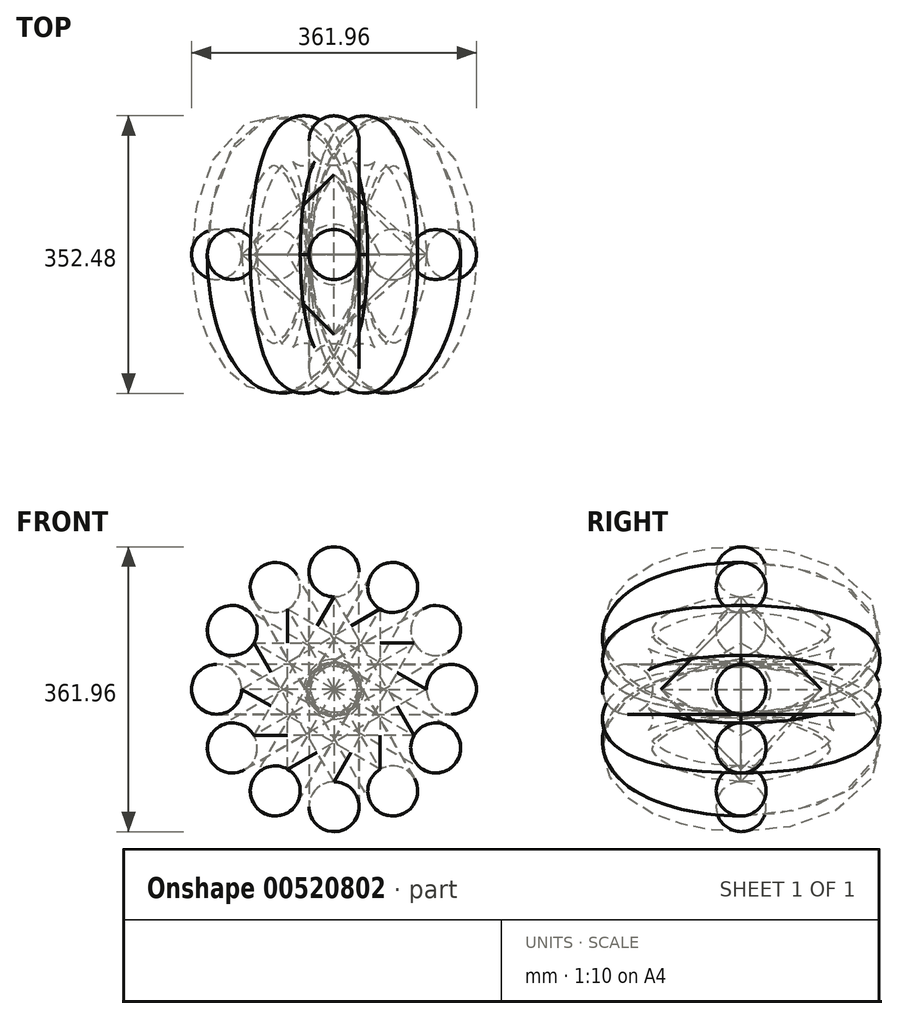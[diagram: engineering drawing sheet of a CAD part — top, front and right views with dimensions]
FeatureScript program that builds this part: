
annotation { "Feature Type Name" : "Feature", "Feature Type Description" : "" }
export const myFeature = defineFeature(function(context is Context, id is Id, definition is map)
    precondition{}
    {
        {
            var Q0;
            Q0=qCreatedBy(makeId("Front.planeOp"),FACE);
            var sketch = newSketch(context, id + "F0", { "sketchPlane" : qUnion([Q0])});
            skCircle(sketch, "E0.cCircle", {"center": v(0, 0) * mm, "radius": 180.98 * mm});
            skLineSegment(sketch, "E0.0", {"start": v(48.5, -180.98) * mm, "end": v(-48.5, -180.98) * mm});
            skLineSegment(sketch, "E0.1", {"start": v(-48.5, -180.98) * mm, "end": v(-132.48, -132.48) * mm});
            skLineSegment(sketch, "E0.2", {"start": v(-132.48, -132.48) * mm, "end": v(-180.98, -48.5) * mm});
            skLineSegment(sketch, "E0.3", {"start": v(-180.97, -48.5) * mm, "end": v(-180.98, 48.5) * mm});
            skLineSegment(sketch, "E0.4", {"start": v(-180.97, 48.5) * mm, "end": v(-132.48, 132.48) * mm});
            skLineSegment(sketch, "E0.5", {"start": v(-132.48, 132.48) * mm, "end": v(-48.5, 180.98) * mm});
            skLineSegment(sketch, "E0.6", {"start": v(-48.5, 180.98) * mm, "end": v(48.5, 180.98) * mm});
            skLineSegment(sketch, "E0.7", {"start": v(48.5, 180.97) * mm, "end": v(132.48, 132.48) * mm});
            skLineSegment(sketch, "E0.8", {"start": v(132.48, 132.48) * mm, "end": v(180.98, 48.5) * mm});
            skLineSegment(sketch, "E0.9", {"start": v(180.98, 48.5) * mm, "end": v(180.98, -48.5) * mm});
            skLineSegment(sketch, "E0.10", {"start": v(180.98, -48.5) * mm, "end": v(132.48, -132.48) * mm});
            skLineSegment(sketch, "E0.11", {"start": v(132.48, -132.48) * mm, "end": v(48.5, -180.98) * mm});
            skPoint(sketch, "E0.0.midPoint", {"position": v(0, -180.98) * mm});
            skCircle(sketch, "E1", {"center": v(0, 0) * mm, "radius": 117.48 * mm});
            skCircle(sketch, "E2", {"center": v(0, 0) * mm, "radius": 149.23 * mm});
            skCircle(sketch, "E3", {"center": v(0, 149.23) * mm, "radius": 31.75 * mm});
            skCircle(sketch, "E4.cCircle", {"center": v(0, 0) * mm, "radius": 117.48 * mm, "construction": true});
            skLineSegment(sketch, "E4.0", {"start": v(0, 117.48) * mm, "end": v(101.74, -58.74) * mm});
            skLineSegment(sketch, "E4.1", {"start": v(101.74, -58.74) * mm, "end": v(-101.74, -58.74) * mm});
            skLineSegment(sketch, "E4.2", {"start": v(-101.74, -58.74) * mm, "end": v(0, 117.47) * mm});
            skLineSegment(sketch, "E5.1.0", {"start": v(-117.48, 0) * mm, "end": v(58.74, 101.74) * mm});
            skLineSegment(sketch, "E5.1.1", {"start": v(58.74, -101.74) * mm, "end": v(-117.48, 0) * mm});
            skLineSegment(sketch, "E5.1.2", {"start": v(58.74, 101.74) * mm, "end": v(58.74, -101.74) * mm});
            skLineSegment(sketch, "E5.2.0", {"start": v(0, -117.48) * mm, "end": v(-101.74, 58.74) * mm});
            skLineSegment(sketch, "E5.2.1", {"start": v(101.74, 58.74) * mm, "end": v(0, -117.48) * mm});
            skLineSegment(sketch, "E5.2.2", {"start": v(-101.74, 58.74) * mm, "end": v(101.74, 58.74) * mm});
            skLineSegment(sketch, "E5.3.0", {"start": v(117.48, 0) * mm, "end": v(-58.74, -101.74) * mm});
            skLineSegment(sketch, "E5.3.1", {"start": v(-58.74, 101.74) * mm, "end": v(117.48, 0) * mm});
            skLineSegment(sketch, "E5.3.2", {"start": v(-58.74, -101.74) * mm, "end": v(-58.74, 101.74) * mm});
            skCircle(sketch, "E6.1.0", {"center": v(-74.61, 129.23) * mm, "radius": 31.75 * mm});
            skCircle(sketch, "E6.2.0", {"center": v(-129.23, 74.61) * mm, "radius": 31.75 * mm});
            skCircle(sketch, "E6.3.0", {"center": v(-149.23, 0) * mm, "radius": 31.75 * mm});
            skCircle(sketch, "E6.4.0", {"center": v(-129.23, -74.61) * mm, "radius": 31.75 * mm});
            skCircle(sketch, "E6.5.0", {"center": v(-74.61, -129.23) * mm, "radius": 31.75 * mm});
            skCircle(sketch, "E6.6.0", {"center": v(0, -149.23) * mm, "radius": 31.75 * mm});
            skCircle(sketch, "E6.7.0", {"center": v(74.61, -129.23) * mm, "radius": 31.75 * mm});
            skCircle(sketch, "E6.8.0", {"center": v(129.23, -74.61) * mm, "radius": 31.75 * mm});
            skCircle(sketch, "E6.9.0", {"center": v(149.23, 0) * mm, "radius": 31.75 * mm});
            skCircle(sketch, "E6.10.0", {"center": v(129.23, 74.61) * mm, "radius": 31.75 * mm});
            skCircle(sketch, "E6.11.0", {"center": v(74.61, 129.23) * mm, "radius": 31.75 * mm});
            skLineSegment(sketch, "E7.bottom", {"start": v(-117.47, 117.48) * mm, "end": v(117.48, 117.48) * mm});
            skLineSegment(sketch, "E7.top", {"start": v(-117.48, -117.48) * mm, "end": v(117.47, -117.48) * mm});
            skLineSegment(sketch, "E7.left", {"start": v(-117.47, 117.48) * mm, "end": v(-117.48, -117.48) * mm});
            skLineSegment(sketch, "E7.right", {"start": v(117.48, 117.48) * mm, "end": v(117.47, -117.48) * mm});
            skCircle(sketch, "E8", {"center": v(0, 0) * mm, "radius": 31.75 * mm});
            skLineSegment(sketch, "E9", {"start": v(0, 117.48) * mm, "end": v(0, 180.98) * mm});
            skSolve(sketch);
        }
        {
            var Q0;
            {var subQ0=sQuery(id+"F0.wireOp",EDGE,"E3");var subQ1=sQuery(id+"F0.wireOp",EDGE,"E2");var subQ2=makeQuery(id+"F0.imprint","INTERSECT",VERTEX,{"disambiguationData":[OD(0.0)],"derivedFrom":[subQ1,subQ0]});Q0=makeQuery(id+"F0.imprint","IMPRINT",FACE,{"disambiguationData":[TD([[makeQuery(id+"F0.imprint","IMPRINT",EDGE,{"disambiguationData":[TD([[subQ2,-1.0]])],"derivedFrom":subQ1}),1.0]])]});}
            var Q1;
            {var subQ0=sQuery(id+"F0.wireOp",EDGE,"E3");var subQ1=sQuery(id+"F0.wireOp",EDGE,"E2");var subQ2=makeQuery(id+"F0.imprint","INTERSECT",VERTEX,{"disambiguationData":[OD(0.0)],"derivedFrom":[subQ1,subQ0]});Q1=makeQuery(id+"F0.imprint","IMPRINT",FACE,{"disambiguationData":[TD([[makeQuery(id+"F0.imprint","IMPRINT",EDGE,{"disambiguationData":[TD([[subQ2,-1.0]])],"derivedFrom":subQ1}),-1.0]])]});}
            var Q2;
            Q2=sQuery(id+"F0.wireOp",EDGE,"E9");
            revolve(context, id + "F1", {"entities" : qUnion([Q0, Q1]), "axis" : qUnion([Q2]), "revolveType" : RevolveType.FULL});
        }
        {
            var Q0;
            Q0=makeQuery(id+"F0.imprint","IMPRINT",FACE,{"disambiguationData":[TD([[makeQuery(id+"F0.imprint","IMPRINT",EDGE,{"derivedFrom":sQuery(id+"F0.wireOp",EDGE,"E8")}),-1.0]])]});
            var Q1;
            {var subQ0=sQuery(id+"F0.wireOp",EDGE,"E5.2.2");var subQ1=sQuery(id+"F0.wireOp",EDGE,"E4.2");var subQ2=makeQuery(id+"F0.imprint","INTERSECT",VERTEX,{"derivedFrom":[subQ1,subQ0]});Q1=makeQuery(id+"F0.imprint","IMPRINT",FACE,{"disambiguationData":[TD([[makeQuery(id+"F0.imprint","IMPRINT",EDGE,{"disambiguationData":[TD([[subQ2,-1.0]])],"derivedFrom":subQ1}),-1.0]])]});}
            var Q2;
            {var subQ1=sQuery(id+"F0.wireOp",EDGE,"E4.0");var subQ3=sQuery(id+"F0.wireOp",EDGE,"E5.1.0");var subQ4=makeQuery(id+"F0.imprint","INTERSECT",VERTEX,{"derivedFrom":[subQ1,subQ3]});Q2=makeQuery(id+"F0.imprint","IMPRINT",FACE,{"disambiguationData":[TD([[makeQuery(id+"F0.imprint","IMPRINT",EDGE,{"disambiguationData":[TD([[subQ4,1.0]])],"derivedFrom":subQ3}),1.0]])]});}
            var Q3;
            {var subQ0=sQuery(id+"F0.wireOp",EDGE,"E5.1.0");var subQ1=sQuery(id+"F0.wireOp",EDGE,"E4.0");var subQ2=makeQuery(id+"F0.imprint","INTERSECT",VERTEX,{"derivedFrom":[subQ1,subQ0]});Q3=makeQuery(id+"F0.imprint","IMPRINT",FACE,{"disambiguationData":[TD([[makeQuery(id+"F0.imprint","IMPRINT",EDGE,{"disambiguationData":[TD([[subQ2,-1.0]])],"derivedFrom":subQ1}),-1.0]])]});}
            var Q4;
            {var subQ0=sQuery(id+"F0.wireOp",EDGE,"E5.2.2");var subQ1=sQuery(id+"F0.wireOp",EDGE,"E4.0");var subQ2=makeQuery(id+"F0.imprint","INTERSECT",VERTEX,{"derivedFrom":[subQ1,subQ0]});Q4=makeQuery(id+"F0.imprint","IMPRINT",FACE,{"disambiguationData":[TD([[makeQuery(id+"F0.imprint","IMPRINT",EDGE,{"disambiguationData":[TD([[subQ2,-1.0]])],"derivedFrom":subQ1}),-1.0]])]});}
            var Q5;
            {var subQ0=sQuery(id+"F0.wireOp",EDGE,"E5.2.2");var subQ1=sQuery(id+"F0.wireOp",EDGE,"E5.1.0");var subQ2=makeQuery(id+"F0.imprint","INTERSECT",VERTEX,{"derivedFrom":[subQ1,subQ0]});Q5=makeQuery(id+"F0.imprint","IMPRINT",FACE,{"disambiguationData":[TD([[makeQuery(id+"F0.imprint","IMPRINT",EDGE,{"disambiguationData":[TD([[subQ2,-1.0]])],"derivedFrom":subQ1}),-1.0]])]});}
            var Q6;
            {var subQ0=sQuery(id+"F0.wireOp",EDGE,"E5.1.0");var subQ1=sQuery(id+"F0.wireOp",EDGE,"E4.2");var subQ2=makeQuery(id+"F0.imprint","INTERSECT",VERTEX,{"derivedFrom":[subQ1,subQ0]});Q6=makeQuery(id+"F0.imprint","IMPRINT",FACE,{"disambiguationData":[TD([[makeQuery(id+"F0.imprint","IMPRINT",EDGE,{"disambiguationData":[TD([[subQ2,-1.0]])],"derivedFrom":subQ1}),-1.0]])]});}
            var Q7;
            {var subQ0=sQuery(id+"F0.wireOp",EDGE,"E5.2.0");var subQ1=sQuery(id+"F0.wireOp",EDGE,"E4.2");var subQ2=makeQuery(id+"F0.imprint","INTERSECT",VERTEX,{"derivedFrom":[subQ1,subQ0]});Q7=makeQuery(id+"F0.imprint","IMPRINT",FACE,{"disambiguationData":[TD([[makeQuery(id+"F0.imprint","IMPRINT",EDGE,{"disambiguationData":[TD([[subQ2,-1.0]])],"derivedFrom":subQ1}),-1.0]])]});}
            var Q8;
            {var subQ0=sQuery(id+"F0.wireOp",EDGE,"E5.1.1");var subQ1=sQuery(id+"F0.wireOp",EDGE,"E4.2");var subQ2=makeQuery(id+"F0.imprint","INTERSECT",VERTEX,{"derivedFrom":[subQ1,subQ0]});Q8=makeQuery(id+"F0.imprint","IMPRINT",FACE,{"disambiguationData":[TD([[makeQuery(id+"F0.imprint","IMPRINT",EDGE,{"disambiguationData":[TD([[subQ2,-1.0]])],"derivedFrom":subQ1}),-1.0]])]});}
            var Q9;
            {var subQ0=sQuery(id+"F0.wireOp",EDGE,"E4.2");var subQ5=sQuery(id+"F0.wireOp",EDGE,"E5.1.1");var subQ6=makeQuery(id+"F0.imprint","INTERSECT",VERTEX,{"derivedFrom":[subQ0,subQ5]});Q9=makeQuery(id+"F0.imprint","IMPRINT",FACE,{"disambiguationData":[TD([[makeQuery(id+"F0.imprint","IMPRINT",EDGE,{"disambiguationData":[TD([[subQ6,1.0]])],"derivedFrom":subQ5}),1.0]])]});}
            var Q10;
            {var subQ0=sQuery(id+"F0.wireOp",EDGE,"E5.2.0");var subQ1=sQuery(id+"F0.wireOp",EDGE,"E4.1");var subQ2=makeQuery(id+"F0.imprint","INTERSECT",VERTEX,{"derivedFrom":[subQ1,subQ0]});Q10=makeQuery(id+"F0.imprint","IMPRINT",FACE,{"disambiguationData":[TD([[makeQuery(id+"F0.imprint","IMPRINT",EDGE,{"disambiguationData":[TD([[subQ2,-1.0]])],"derivedFrom":subQ1}),-1.0]])]});}
            var Q11;
            {var subQ0=sQuery(id+"F0.wireOp",EDGE,"E5.1.1");var subQ1=sQuery(id+"F0.wireOp",EDGE,"E4.1");var subQ2=makeQuery(id+"F0.imprint","INTERSECT",VERTEX,{"derivedFrom":[subQ1,subQ0]});Q11=makeQuery(id+"F0.imprint","IMPRINT",FACE,{"disambiguationData":[TD([[makeQuery(id+"F0.imprint","IMPRINT",EDGE,{"disambiguationData":[TD([[subQ2,-1.0]])],"derivedFrom":subQ1}),-1.0]])]});}
            var Q12;
            {var subQ0=sQuery(id+"F0.wireOp",EDGE,"E5.1.2");var subQ1=sQuery(id+"F0.wireOp",EDGE,"E4.1");var subQ2=makeQuery(id+"F0.imprint","INTERSECT",VERTEX,{"derivedFrom":[subQ1,subQ0]});Q12=makeQuery(id+"F0.imprint","IMPRINT",FACE,{"disambiguationData":[TD([[makeQuery(id+"F0.imprint","IMPRINT",EDGE,{"disambiguationData":[TD([[subQ2,-1.0]])],"derivedFrom":subQ1}),-1.0]])]});}
            var Q13;
            {var subQ0=sQuery(id+"F0.wireOp",EDGE,"E5.2.1");var subQ1=sQuery(id+"F0.wireOp",EDGE,"E4.1");var subQ2=makeQuery(id+"F0.imprint","INTERSECT",VERTEX,{"derivedFrom":[subQ1,subQ0]});Q13=makeQuery(id+"F0.imprint","IMPRINT",FACE,{"disambiguationData":[TD([[makeQuery(id+"F0.imprint","IMPRINT",EDGE,{"disambiguationData":[TD([[subQ2,-1.0]])],"derivedFrom":subQ1}),-1.0]])]});}
            var Q14;
            {var subQ0=sQuery(id+"F0.wireOp",EDGE,"E4.1");var subQ5=sQuery(id+"F0.wireOp",EDGE,"E5.1.2");var subQ6=makeQuery(id+"F0.imprint","INTERSECT",VERTEX,{"derivedFrom":[subQ0,subQ5]});Q14=makeQuery(id+"F0.imprint","IMPRINT",FACE,{"disambiguationData":[TD([[makeQuery(id+"F0.imprint","IMPRINT",EDGE,{"disambiguationData":[TD([[subQ6,1.0]])],"derivedFrom":subQ5}),1.0]])]});}
            var Q15;
            {var subQ0=sQuery(id+"F0.wireOp",EDGE,"E5.2.1");var subQ1=sQuery(id+"F0.wireOp",EDGE,"E4.0");var subQ2=makeQuery(id+"F0.imprint","INTERSECT",VERTEX,{"derivedFrom":[subQ1,subQ0]});Q15=makeQuery(id+"F0.imprint","IMPRINT",FACE,{"disambiguationData":[TD([[makeQuery(id+"F0.imprint","IMPRINT",EDGE,{"disambiguationData":[TD([[subQ2,-1.0]])],"derivedFrom":subQ1}),-1.0]])]});}
            var Q16;
            {var subQ0=sQuery(id+"F0.wireOp",EDGE,"E5.1.2");var subQ1=sQuery(id+"F0.wireOp",EDGE,"E4.0");var subQ2=makeQuery(id+"F0.imprint","INTERSECT",VERTEX,{"derivedFrom":[subQ1,subQ0]});Q16=makeQuery(id+"F0.imprint","IMPRINT",FACE,{"disambiguationData":[TD([[makeQuery(id+"F0.imprint","IMPRINT",EDGE,{"disambiguationData":[TD([[subQ2,-1.0]])],"derivedFrom":subQ1}),-1.0]])]});}
            var Q17;
            {var subQ0=sQuery(id+"F0.wireOp",EDGE,"E5.2.0");var subQ1=sQuery(id+"F0.wireOp",EDGE,"E5.1.1");var subQ2=makeQuery(id+"F0.imprint","INTERSECT",VERTEX,{"derivedFrom":[subQ1,subQ0]});Q17=makeQuery(id+"F0.imprint","IMPRINT",FACE,{"disambiguationData":[TD([[makeQuery(id+"F0.imprint","IMPRINT",EDGE,{"disambiguationData":[TD([[subQ2,-1.0]])],"derivedFrom":subQ1}),-1.0]])]});}
            var Q18;
            {var subQ0=sQuery(id+"F0.wireOp",EDGE,"E5.2.1");var subQ1=sQuery(id+"F0.wireOp",EDGE,"E5.1.2");var subQ2=makeQuery(id+"F0.imprint","INTERSECT",VERTEX,{"derivedFrom":[subQ1,subQ0]});Q18=makeQuery(id+"F0.imprint","IMPRINT",FACE,{"disambiguationData":[TD([[makeQuery(id+"F0.imprint","IMPRINT",EDGE,{"disambiguationData":[TD([[subQ2,-1.0]])],"derivedFrom":subQ1}),-1.0]])]});}
            var Q19;
            Q19=makeQuery(id+"F0.imprint","IMPRINT",FACE,{"disambiguationData":[TD([[makeQuery(id+"F0.imprint","IMPRINT",EDGE,{"derivedFrom":sQuery(id+"F0.wireOp",EDGE,"E8")}),1.0]])]});
            extrude(context, id + "F2", {"entities" : qUnion([Q0, Q1, Q2, Q3, Q4, Q5, Q6, Q7, Q8, Q9, Q10, Q11, Q12, Q13, Q14, Q15, Q16, Q17, Q18, Q19]), "endBound" : BoundingType.SYMMETRIC, "depth" : 254 * mm, "offsetDistance" : 25.4 * mm, "hasDraft" : true, "draftAngle" : 30 * degree, "draftPullDirection" : true});
        }
        {
            var Q0;
            Q0=qCreatedBy(makeId("Top.planeOp"),FACE);
            var sketch = newSketch(context, id + "F3", { "sketchPlane" : qUnion([Q0])});
            skLineSegment(sketch, "E10", {"start": v(0, -108.49) * mm, "end": v(0, 108.76) * mm, "construction": true});
            skLineSegment(sketch, "E11", {"start": v(-196.05, 0) * mm, "end": v(191.93, 0) * mm, "construction": true});
            skSolve(sketch);
        }
        {
            var Q0;
            Q0=makeQuery(id+"F1.opRevolve","SWEPT_BODY",BODY,{"disambiguationData":[OSD([sQuery(id+"F0.wireOp",EDGE,"E3"),sQuery(id+"F0.wireOp",EDGE,"E9")])]});
            var Q1;
            Q1=sQuery(id+"F3.wireOp",EDGE,"E10");
            circularPattern(context, id + "F4", {"entities" : qUnion([Q0]), "axis" : qUnion([Q1]), "angle" : 360 * degree, "instanceCount" : 12, "equalSpace" : true});
        }
        {
            var Q0;
            Q0=makeQuery(id+"F2.*.split.splitOp","SPLIT",BODY,{"derivedFrom":makeQuery(id+"F2.opExtrude","SWEPT_BODY",BODY,{"disambiguationData":[OSD([sQuery(id+"F0.wireOp",EDGE,"E4.0"),sQuery(id+"F0.wireOp",EDGE,"E4.1"),sQuery(id+"F0.wireOp",EDGE,"E4.2")])]})});
            var Q1;
            Q1=sQuery(id+"F3.wireOp",EDGE,"E10");
            circularPattern(context, id + "F5", {"entities" : qUnion([Q0]), "axis" : qUnion([Q1]), "angle" : 360 * degree, "instanceCount" : 4, "equalSpace" : true});
        }
        {
            var Q0;
            Q0=qCreatedBy(makeId("Top.planeOp"),FACE);
            var sketch = newSketch(context, id + "F6", { "sketchPlane" : qUnion([Q0])});
            skCircle(sketch, "E12.cCircle", {"center": v(0, 0) * mm, "radius": 182.8 * mm});
            skLineSegment(sketch, "E12.0", {"start": v(48.98, -182.8) * mm, "end": v(-48.98, -182.8) * mm});
            skLineSegment(sketch, "E12.1", {"start": v(-48.98, -182.8) * mm, "end": v(-133.82, -133.82) * mm});
            skLineSegment(sketch, "E12.2", {"start": v(-133.82, -133.82) * mm, "end": v(-182.8, -48.98) * mm});
            skLineSegment(sketch, "E12.3", {"start": v(-182.8, -48.98) * mm, "end": v(-182.8, 48.98) * mm});
            skLineSegment(sketch, "E12.4", {"start": v(-182.8, 48.98) * mm, "end": v(-133.82, 133.82) * mm});
            skLineSegment(sketch, "E12.5", {"start": v(-133.82, 133.82) * mm, "end": v(-48.98, 182.8) * mm});
            skLineSegment(sketch, "E12.6", {"start": v(-48.98, 182.8) * mm, "end": v(48.98, 182.8) * mm});
            skLineSegment(sketch, "E12.7", {"start": v(48.98, 182.8) * mm, "end": v(133.82, 133.82) * mm});
            skLineSegment(sketch, "E12.8", {"start": v(133.82, 133.82) * mm, "end": v(182.8, 48.98) * mm});
            skLineSegment(sketch, "E12.9", {"start": v(182.8, 48.98) * mm, "end": v(182.8, -48.98) * mm});
            skLineSegment(sketch, "E12.10", {"start": v(182.8, -48.98) * mm, "end": v(133.82, -133.82) * mm});
            skLineSegment(sketch, "E12.11", {"start": v(133.82, -133.82) * mm, "end": v(48.98, -182.8) * mm});
            skPoint(sketch, "E12.0.midPoint", {"position": v(0, -182.8) * mm});
            skCircle(sketch, "E13", {"center": v(0, 0) * mm, "radius": 117.48 * mm});
            skCircle(sketch, "E14", {"center": v(0, 0) * mm, "radius": 149.23 * mm});
            skCircle(sketch, "E15", {"center": v(0, 149.23) * mm, "radius": 31.75 * mm});
            skCircle(sketch, "E16.cCircle", {"center": v(0, 0) * mm, "radius": 117.48 * mm, "construction": true});
            skLineSegment(sketch, "E16.0", {"start": v(0, 117.48) * mm, "end": v(101.74, -58.74) * mm});
            skLineSegment(sketch, "E16.1", {"start": v(101.74, -58.74) * mm, "end": v(-101.74, -58.74) * mm});
            skLineSegment(sketch, "E16.2", {"start": v(-101.74, -58.74) * mm, "end": v(0, 117.47) * mm});
            skLineSegment(sketch, "E17.1.0", {"start": v(-117.48, 0) * mm, "end": v(58.74, 101.74) * mm});
            skLineSegment(sketch, "E17.1.1", {"start": v(58.74, -101.74) * mm, "end": v(-117.48, 0) * mm});
            skLineSegment(sketch, "E17.1.2", {"start": v(58.74, 101.74) * mm, "end": v(58.74, -101.74) * mm});
            skLineSegment(sketch, "E17.2.0", {"start": v(0, -117.48) * mm, "end": v(-101.74, 58.74) * mm});
            skLineSegment(sketch, "E17.2.1", {"start": v(101.74, 58.74) * mm, "end": v(0, -117.48) * mm});
            skLineSegment(sketch, "E17.2.2", {"start": v(-101.74, 58.74) * mm, "end": v(101.74, 58.74) * mm});
            skLineSegment(sketch, "E17.3.0", {"start": v(117.48, 0) * mm, "end": v(-58.74, -101.74) * mm});
            skLineSegment(sketch, "E17.3.1", {"start": v(-58.74, 101.74) * mm, "end": v(117.48, 0) * mm});
            skLineSegment(sketch, "E17.3.2", {"start": v(-58.74, -101.74) * mm, "end": v(-58.74, 101.74) * mm});
            skCircle(sketch, "E18.1.0", {"center": v(-74.61, 129.23) * mm, "radius": 31.75 * mm});
            skCircle(sketch, "E18.2.0", {"center": v(-129.23, 74.61) * mm, "radius": 31.75 * mm});
            skCircle(sketch, "E18.3.0", {"center": v(-149.23, 0) * mm, "radius": 31.75 * mm});
            skCircle(sketch, "E18.4.0", {"center": v(-129.23, -74.61) * mm, "radius": 31.75 * mm});
            skCircle(sketch, "E18.5.0", {"center": v(-74.61, -129.23) * mm, "radius": 31.75 * mm});
            skCircle(sketch, "E18.6.0", {"center": v(0, -149.23) * mm, "radius": 31.75 * mm});
            skCircle(sketch, "E18.7.0", {"center": v(74.61, -129.23) * mm, "radius": 31.75 * mm});
            skCircle(sketch, "E18.8.0", {"center": v(129.23, -74.61) * mm, "radius": 31.75 * mm});
            skCircle(sketch, "E18.9.0", {"center": v(149.23, 0) * mm, "radius": 31.75 * mm});
            skCircle(sketch, "E18.10.0", {"center": v(129.23, 74.61) * mm, "radius": 31.75 * mm});
            skCircle(sketch, "E18.11.0", {"center": v(74.61, 129.23) * mm, "radius": 31.75 * mm});
            skLineSegment(sketch, "E19.bottom", {"start": v(-117.47, 117.48) * mm, "end": v(117.48, 117.48) * mm});
            skLineSegment(sketch, "E19.top", {"start": v(-117.48, -117.48) * mm, "end": v(117.47, -117.48) * mm});
            skLineSegment(sketch, "E19.left", {"start": v(-117.47, 117.48) * mm, "end": v(-117.48, -117.48) * mm});
            skLineSegment(sketch, "E19.right", {"start": v(117.48, 117.48) * mm, "end": v(117.47, -117.48) * mm});
            skCircle(sketch, "E20", {"center": v(0, 0) * mm, "radius": 31.75 * mm});
            skSolve(sketch);
        }
        {
            var Q0;
            Q0=qCreatedBy(makeId("Top.planeOp"),FACE);
            var sketch = newSketch(context, id + "F7", { "sketchPlane" : qUnion([Q0])});
            skLineSegment(sketch, "E21", {"start": v(0, 0) * mm, "end": v(-152.4, 0) * mm, "construction": true});
            skEllipse(sketch, "E22", {"center": v(-76.2, 0) * mm, "majorRadius": 76.2 * mm, "minorRadius": 147.66 * mm, "majorAxis": v(1, 0)});
            skSolve(sketch);
        }
        {
            var Q0;
            {var subQ0=sQuery(id+"F0.wireOp",EDGE,"E6.3.0");var subQ1=sQuery(id+"F0.wireOp",EDGE,"E2");var subQ2=makeQuery(id+"F0.imprint","INTERSECT",VERTEX,{"disambiguationData":[OD(0.0)],"derivedFrom":[subQ1,subQ0]});Q0=makeQuery(id+"F0.imprint","IMPRINT",FACE,{"disambiguationData":[TD([[makeQuery(id+"F0.imprint","IMPRINT",EDGE,{"disambiguationData":[TD([[subQ2,-1.0]])],"derivedFrom":subQ1}),-1.0]])]});}
            var Q1;
            {var subQ0=sQuery(id+"F0.wireOp",EDGE,"E6.3.0");var subQ1=sQuery(id+"F0.wireOp",EDGE,"E2");var subQ2=makeQuery(id+"F0.imprint","INTERSECT",VERTEX,{"disambiguationData":[OD(0.0)],"derivedFrom":[subQ1,subQ0]});Q1=makeQuery(id+"F0.imprint","IMPRINT",FACE,{"disambiguationData":[TD([[makeQuery(id+"F0.imprint","IMPRINT",EDGE,{"disambiguationData":[TD([[subQ2,-1.0]])],"derivedFrom":subQ1}),1.0]])]});}
            var Q2;
            Q2=sQuery(id+"F0.wireOp",EDGE,"E6.3.0");
            var Q3;
            Q3=sQuery(id+"F7.wireOp",EDGE,"E22");
            sweep(context, id + "F8", {"profiles" : qUnion([Q0, Q1]), "surfaceProfiles" : qUnion([Q2]), "path" : qUnion([Q3])});
        }
        {
            var Q0;
            Q0=makeQuery(id+"F8.opSweep","SWEPT_BODY",BODY,{"disambiguationData":[OSD([sQuery(id+"F0.wireOp",EDGE,"E6.3.0"),sQuery(id+"F7.wireOp",EDGE,"E22")])]});
            var Q1;
            Q1=sQuery(id+"F3.wireOp",EDGE,"E10");
            circularPattern(context, id + "F9", {"entities" : qUnion([Q0]), "axis" : qUnion([Q1]), "angle" : 360 * degree, "instanceCount" : 12, "equalSpace" : true});
        }
        {
            var Q0;
            Q0=qCreatedBy(makeId("Front.planeOp"),FACE);
            var sketch = newSketch(context, id + "F10", { "sketchPlane" : qUnion([Q0])});
            skCircle(sketch, "E23", {"center": v(0, 0) * mm, "radius": 38.1 * mm});
            skLineSegment(sketch, "E24", {"start": v(0, 38.1) * mm, "end": v(0, -38.1) * mm});
            skSolve(sketch);
        }
        {
            var Q0;
            {var subQ0=sQuery(id+"F10.wireOp",EDGE,"E24");Q0=makeQuery(id+"F10.imprint","IMPRINT",FACE,{"disambiguationData":[TD([[makeQuery(id+"F10.imprint","IMPRINT",EDGE,{"derivedFrom":subQ0}),-1.0]])]});}
            var Q1;
            Q1=sQuery(id+"F10.wireOp",EDGE,"E24");
            revolve(context, id + "F11", {"entities" : qUnion([Q0]), "axis" : qUnion([Q1]), "revolveType" : RevolveType.TWO_DIRECTIONS, "angle" : 0 * degree, "angleBack" : 180 * degree});
        }
        {
            var Q0;
            {var subQ0=sQuery(id+"F10.wireOp",EDGE,"E24");Q0=makeQuery(id+"F10.imprint","IMPRINT",FACE,{"disambiguationData":[TD([[makeQuery(id+"F10.imprint","IMPRINT",EDGE,{"derivedFrom":subQ0}),-1.0]])]});}
            var Q1;
            Q1=sQuery(id+"F10.wireOp",EDGE,"E24");
            revolve(context, id + "F12", {"entities" : qUnion([Q0]), "axis" : qUnion([Q1]), "revolveType" : RevolveType.ONE_DIRECTION, "angle" : 180 * degree});
        }
    });
